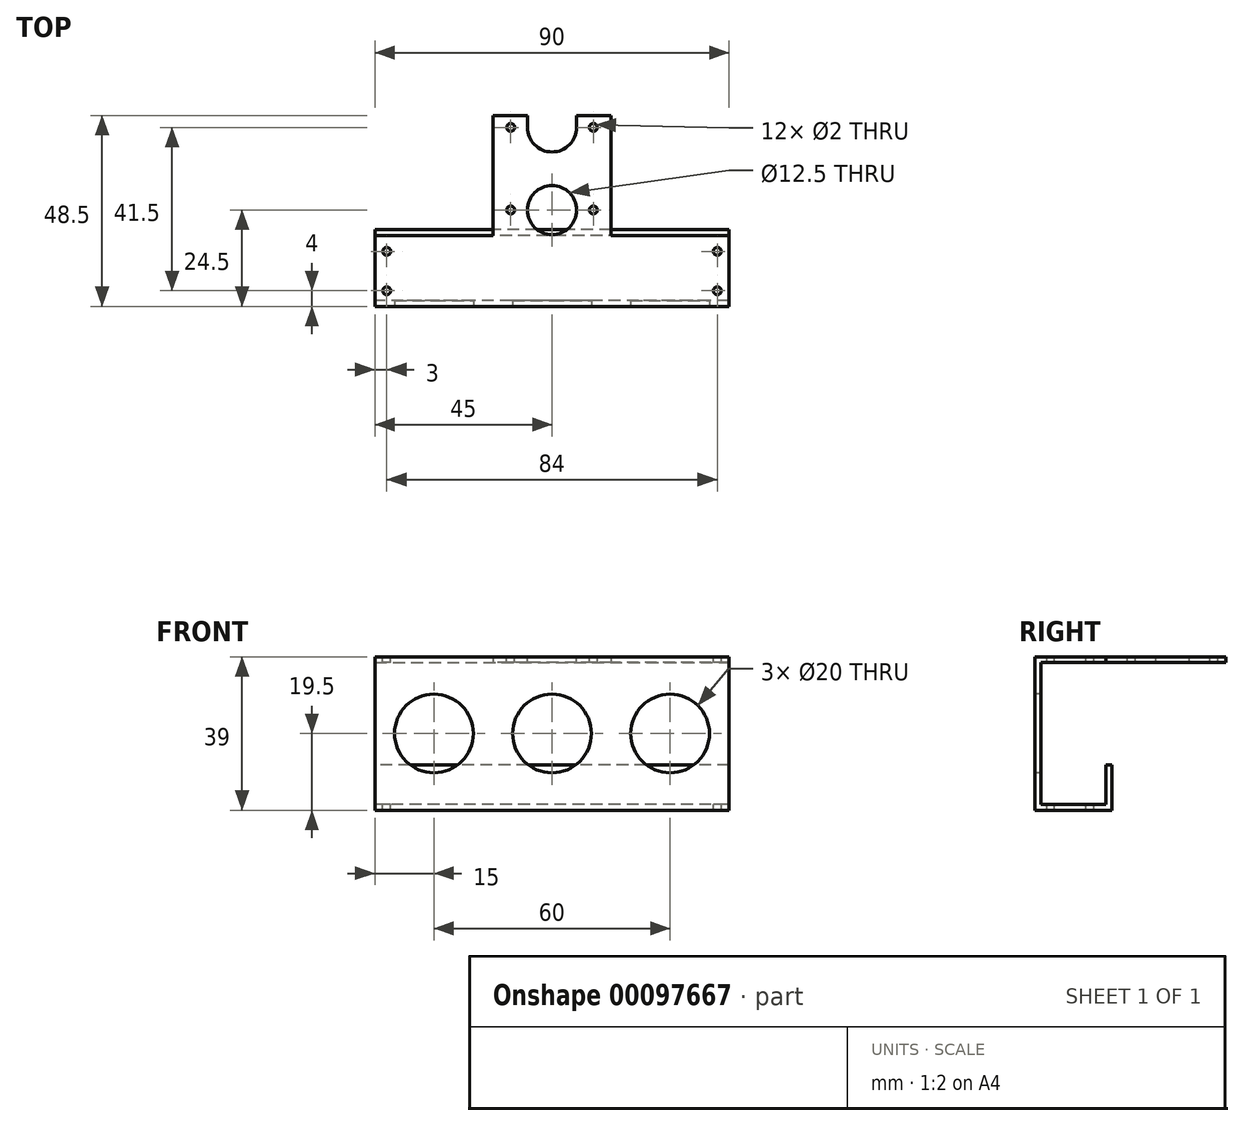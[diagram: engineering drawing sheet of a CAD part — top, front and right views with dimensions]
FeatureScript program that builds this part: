
annotation { "Feature Type Name" : "Feature", "Feature Type Description" : "" }
export const myFeature = defineFeature(function(context is Context, id is Id, definition is map)
    precondition{}
    {
        {
            var Q0;
            Q0=qCreatedBy(makeId("Top.planeOp"),FACE);
            var sketch = newSketch(context, id + "F0", { "sketchPlane" : qUnion([Q0])});
            skLineSegment(sketch, "E0.bottom", {"start": v(15, -24.25) * mm, "end": v(-15, -24.25) * mm});
            skLineSegment(sketch, "E0.top", {"start": v(15, 24.25) * mm, "end": v(-15, 24.25) * mm});
            skLineSegment(sketch, "E0.left", {"start": v(15, -24.25) * mm, "end": v(15, 24.25) * mm});
            skLineSegment(sketch, "E0.right", {"start": v(-15, -24.25) * mm, "end": v(-15, 24.25) * mm});
            skPoint(sketch, "E0.middle", {"position": v(0, 0) * mm});
            skSolve(sketch);
        }
        {
            var Q0;
            Q0 = qSketchRegion(id + "F0", true);
            extrude(context, id + "F1", {"entities" : qUnion([Q0]), "depth" : 1.5 * mm});
        }
        {
            var Q0;
            Q0=makeQuery(id+"F1.opExtrude","CAP_FACE",FACE,{"disambiguationData":[OSD([sQuery(id+"F0.wireOp",EDGE,"E0.bottom"),sQuery(id+"F0.wireOp",EDGE,"E0.top"),sQuery(id+"F0.wireOp",EDGE,"E0.left"),sQuery(id+"F0.wireOp",EDGE,"E0.right")])],"isStart":true});
            var sketch = newSketch(context, id + "F2", { "sketchPlane" : qUnion([Q0])});
            skLineSegment(sketch, "E1.bottom", {"start": v(-15, 24.25) * mm, "end": v(15, 24.25) * mm});
            skLineSegment(sketch, "E1.top", {"start": v(-15, 22.75) * mm, "end": v(15, 22.75) * mm});
            skLineSegment(sketch, "E1.left", {"start": v(-15, 24.25) * mm, "end": v(-15, 22.75) * mm});
            skLineSegment(sketch, "E1.right", {"start": v(15, 24.25) * mm, "end": v(15, 22.75) * mm});
            skSolve(sketch);
        }
        {
            var Q0;
            Q0 = qSketchRegion(id + "F2", true);
            extrude(context, id + "F3", {"entities" : qUnion([Q0]), "operationType" : NewBodyOperationType.ADD, "depth" : 37.5 * mm});
        }
        {
            var Q0;
            Q0=makeQuery(id+"F3.opExtrude","SWEPT_FACE",FACE,{"disambiguationData":[OSD([sQuery(id+"F2.wireOp",EDGE,"E1.top")])]});
            var sketch = newSketch(context, id + "F4", { "sketchPlane" : qUnion([Q0])});
            skLineSegment(sketch, "E2.bottom", {"start": v(-15, -37.5) * mm, "end": v(15, -37.5) * mm});
            skLineSegment(sketch, "E2.top", {"start": v(-15, -36) * mm, "end": v(15, -36) * mm});
            skLineSegment(sketch, "E2.left", {"start": v(-15, -37.5) * mm, "end": v(-15, -36) * mm});
            skLineSegment(sketch, "E2.right", {"start": v(15, -37.5) * mm, "end": v(15, -36) * mm});
            skSolve(sketch);
        }
        {
            var Q0;
            Q0 = qSketchRegion(id + "F4", true);
            extrude(context, id + "F5", {"entities" : qUnion([Q0]), "operationType" : NewBodyOperationType.ADD, "depth" : 18 * mm});
        }
        {
            var Q0;
            Q0=makeQuery(id+"F5.opExtrude","SWEPT_FACE",FACE,{"disambiguationData":[OSD([sQuery(id+"F4.wireOp",EDGE,"E2.top")])]});
            var sketch = newSketch(context, id + "F6", { "sketchPlane" : qUnion([Q0])});
            skLineSegment(sketch, "E3.bottom", {"start": v(15, -4.75) * mm, "end": v(-15, -4.75) * mm});
            skLineSegment(sketch, "E3.top", {"start": v(15, -6.25) * mm, "end": v(-15, -6.25) * mm});
            skLineSegment(sketch, "E3.left", {"start": v(15, -4.75) * mm, "end": v(15, -6.25) * mm});
            skLineSegment(sketch, "E3.right", {"start": v(-15, -4.75) * mm, "end": v(-15, -6.25) * mm});
            skSolve(sketch);
        }
        {
            var Q0;
            Q0 = qSketchRegion(id + "F6", true);
            extrude(context, id + "F7", {"entities" : qUnion([Q0]), "operationType" : NewBodyOperationType.ADD, "depth" : 10 * mm});
        }
        {
            var Q0;
            Q0=makeQuery(id+"F7.boolean.opBoolean","MERGE",FACE,{"derivedFrom":[makeQuery(id+"F5.boolean.opBoolean","MERGE",FACE,{"derivedFrom":[makeQuery(id+"F3.boolean.opBoolean","MERGE",FACE,{"derivedFrom":[makeQuery(id+"F1.opExtrude","SWEPT_FACE",FACE,{"disambiguationData":[OSD([sQuery(id+"F0.wireOp",EDGE,"E0.left")])]}),makeQuery(id+"F3.opExtrude","SWEPT_FACE",FACE,{"disambiguationData":[OSD([sQuery(id+"F2.wireOp",EDGE,"E1.right")])]})]}),makeQuery(id+"F5.opExtrude","SWEPT_FACE",FACE,{"disambiguationData":[OSD([sQuery(id+"F4.wireOp",EDGE,"E2.left")])]})]}),makeQuery(id+"F7.opExtrude","SWEPT_FACE",FACE,{"disambiguationData":[OSD([sQuery(id+"F6.wireOp",EDGE,"E3.left")])]})]});
            var sketch = newSketch(context, id + "F8", { "sketchPlane" : qUnion([Q0])});
            skLineSegment(sketch, "E4.bottom", {"start": v(-24.25, 1.5) * mm, "end": v(-22.75, 1.5) * mm});
            skLineSegment(sketch, "E4.top", {"start": v(-24.25, -37.5) * mm, "end": v(-22.75, -37.5) * mm});
            skLineSegment(sketch, "E4.left", {"start": v(-24.25, 1.5) * mm, "end": v(-24.25, -37.5) * mm});
            skLineSegment(sketch, "E4.right", {"start": v(-22.75, 0) * mm, "end": v(-22.75, -36) * mm});
            skLineSegment(sketch, "E5.bottom", {"start": v(-6.25, -26) * mm, "end": v(-4.75, -26) * mm});
            skLineSegment(sketch, "E5.top", {"start": v(-6.25, -37.5) * mm, "end": v(-4.75, -37.5) * mm});
            skLineSegment(sketch, "E5.left", {"start": v(-6.25, -26) * mm, "end": v(-6.25, -36) * mm});
            skLineSegment(sketch, "E5.right", {"start": v(-4.75, -26) * mm, "end": v(-4.75, -37.5) * mm});
            skLineSegment(sketch, "E6.bottom", {"start": v(-22.75, -37.5) * mm, "end": v(-2, -37.5) * mm});
            skLineSegment(sketch, "E6.top", {"start": v(-22.75, -36) * mm, "end": v(-6.25, -36) * mm});
            skLineSegment(sketch, "E7.bottom", {"start": v(-22.75, 1.5) * mm, "end": v(-6.25, 1.5) * mm});
            skLineSegment(sketch, "E7.top", {"start": v(-22.75, 0) * mm, "end": v(-6.25, 0) * mm});
            skLineSegment(sketch, "E7.right", {"start": v(-6.25, 1.5) * mm, "end": v(-6.25, 0) * mm});
            skSolve(sketch);
        }
        {
            var Q0;
            Q0 = qSketchRegion(id + "F8", true);
            extrude(context, id + "F9", {"entities" : qUnion([Q0]), "operationType" : NewBodyOperationType.ADD, "depth" : 30 * mm});
        }
        {
            var Q0;
            Q0=makeQuery(id+"F1.opExtrude","SWEPT_BODY",BODY,{"disambiguationData":[OSD([sQuery(id+"F0.wireOp",EDGE,"E0.bottom"),sQuery(id+"F0.wireOp",EDGE,"E0.top"),sQuery(id+"F0.wireOp",EDGE,"E0.left"),sQuery(id+"F0.wireOp",EDGE,"E0.right")])]});
            var Q1;
            Q1=qCreatedBy(makeId("Right.planeOp"),FACE);
            mirror(context, id + "F10", {"operationType" : NewBodyOperationType.ADD, "entities" : qUnion([Q0]), "mirrorPlane" : qUnion([Q1])});
        }
        {
            var Q0;
            {var subQ0=makeQuery(id+"F9.boolean.opBoolean","MERGE",FACE,{"derivedFrom":[makeQuery(id+"F1.opExtrude","CAP_FACE",FACE,{"disambiguationData":[OSD([sQuery(id+"F0.wireOp",EDGE,"E0.bottom"),sQuery(id+"F0.wireOp",EDGE,"E0.top"),sQuery(id+"F0.wireOp",EDGE,"E0.left"),sQuery(id+"F0.wireOp",EDGE,"E0.right")])],"isStart":false}),makeQuery(id+"F9.opExtrude","SWEPT_FACE",FACE,{"disambiguationData":[OSD([sQuery(id+"F8.wireOp",EDGE,"E4.bottom")])]})]});Q0=makeQuery(id+"F10.boolean.opBoolean","MERGE",FACE,{"derivedFrom":[subQ0,makeQuery(id+"F10.opPattern","COPY",FACE,{"derivedFrom":subQ0,"instanceName":"1"})]});}
            var sketch = newSketch(context, id + "F11", { "sketchPlane" : qUnion([Q0])});
            skLineSegment(sketch, "E8", {"start": v(0, 24.25) * mm, "end": v(0, -24.25) * mm, "construction": true});
            skCircle(sketch, "E9", {"center": v(10.5, 21.25) * mm, "radius": 1 * mm});
            skCircle(sketch, "E10", {"center": v(10.5, 0.25) * mm, "radius": 1 * mm});
            skArc(sketch, "E11", {"start": v(-6.25, 21.25) * mm, "mid": v(0, 15) * mm, "end": v(6.25, 21.25) * mm});
            skCircle(sketch, "E12.MirrorC", {"center": v(-10.5, 21.25) * mm, "radius": 1 * mm});
            skCircle(sketch, "E13.MirrorC", {"center": v(-10.5, 0.25) * mm, "radius": 1 * mm});
            skLineSegment(sketch, "E14", {"start": v(-6.25, 21.25) * mm, "end": v(-6.25, 24.25) * mm});
            skLineSegment(sketch, "E15.MirrorCS", {"start": v(6.25, 21.25) * mm, "end": v(6.25, 24.25) * mm});
            skLineSegment(sketch, "E16", {"start": v(-6.25, 24.25) * mm, "end": v(6.25, 24.25) * mm});
            skCircle(sketch, "E17", {"center": v(0, 0.25) * mm, "radius": 6.25 * mm});
            skLineSegment(sketch, "E18", {"start": v(-45, -15.25) * mm, "end": v(45, -15.25) * mm, "construction": true});
            skCircle(sketch, "E19", {"center": v(-42, -10.25) * mm, "radius": 1 * mm});
            skCircle(sketch, "E20.MirrorC", {"center": v(-42, -20.25) * mm, "radius": 1 * mm});
            skCircle(sketch, "E21.MirrorC", {"center": v(42, -10.25) * mm, "radius": 1 * mm});
            skCircle(sketch, "E22.MirrorC", {"center": v(42, -20.25) * mm, "radius": 1 * mm});
            skSolve(sketch);
        }
        {
            var Q0;
            Q0 = qSketchRegion(id + "F11", true);
            extrude(context, id + "F12", {"entities" : qUnion([Q0]), "operationType" : NewBodyOperationType.REMOVE, "endBound" : BoundingType.UP_TO_NEXT, "oppositeDirection" : true, "depth" : 25 * mm});
        }
        {
            var Q0;
            {var subQ0=makeQuery(id+"F9.boolean.opBoolean","MERGE",FACE,{"derivedFrom":[makeQuery(id+"F5.opExtrude","SWEPT_FACE",FACE,{"disambiguationData":[OSD([sQuery(id+"F4.wireOp",EDGE,"E2.top")])]}),makeQuery(id+"F9.opExtrude","SWEPT_FACE",FACE,{"disambiguationData":[OSD([sQuery(id+"F8.wireOp",EDGE,"E6.top")])]})]});Q0=makeQuery(id+"F10.boolean.opBoolean","MERGE",FACE,{"derivedFrom":[subQ0,makeQuery(id+"F10.opPattern","COPY",FACE,{"derivedFrom":subQ0,"instanceName":"1"})]});}
            var sketch = newSketch(context, id + "F13", { "sketchPlane" : qUnion([Q0])});
            skCircle(sketch, "E23.0", {"center": v(-42, -10.25) * mm, "radius": 1 * mm});
            skCircle(sketch, "E24.0", {"center": v(-42, -20.25) * mm, "radius": 1 * mm});
            skCircle(sketch, "E25.0", {"center": v(42, -10.25) * mm, "radius": 1 * mm});
            skCircle(sketch, "E26.0", {"center": v(42, -20.25) * mm, "radius": 1 * mm});
            skSolve(sketch);
        }
        {
            var Q0;
            Q0 = qSketchRegion(id + "F13", true);
            extrude(context, id + "F14", {"entities" : qUnion([Q0]), "operationType" : NewBodyOperationType.REMOVE, "endBound" : BoundingType.UP_TO_NEXT, "oppositeDirection" : true, "depth" : 25 * mm});
        }
        {
            var Q0;
            {var subQ0=makeQuery(id+"F9.boolean.opBoolean","MERGE",FACE,{"derivedFrom":[makeQuery(id+"F3.boolean.opBoolean","MERGE",FACE,{"derivedFrom":[makeQuery(id+"F1.opExtrude","SWEPT_FACE",FACE,{"disambiguationData":[OSD([sQuery(id+"F0.wireOp",EDGE,"E0.bottom")])]}),makeQuery(id+"F3.opExtrude","SWEPT_FACE",FACE,{"disambiguationData":[OSD([sQuery(id+"F2.wireOp",EDGE,"E1.bottom")])]})]}),makeQuery(id+"F9.opExtrude","SWEPT_FACE",FACE,{"disambiguationData":[OSD([sQuery(id+"F8.wireOp",EDGE,"E4.left")])]})]});Q0=makeQuery(id+"F10.boolean.opBoolean","MERGE",FACE,{"derivedFrom":[subQ0,makeQuery(id+"F10.opPattern","COPY",FACE,{"derivedFrom":subQ0,"instanceName":"1"})]});}
            var sketch = newSketch(context, id + "F15", { "sketchPlane" : qUnion([Q0])});
            skLineSegment(sketch, "E27", {"start": v(-45, -18) * mm, "end": v(45, -18) * mm, "construction": true});
            skCircle(sketch, "E28", {"center": v(0, -18) * mm, "radius": 10 * mm});
            skCircle(sketch, "E29", {"center": v(-30, -18) * mm, "radius": 10 * mm});
            skCircle(sketch, "E30.MirrorC", {"center": v(30, -18) * mm, "radius": 10 * mm});
            skSolve(sketch);
        }
        {
            var Q0;
            Q0 = qSketchRegion(id + "F15", true);
            extrude(context, id + "F16", {"entities" : qUnion([Q0]), "operationType" : NewBodyOperationType.REMOVE, "endBound" : BoundingType.UP_TO_NEXT, "oppositeDirection" : true, "depth" : 25 * mm});
        }
    });
